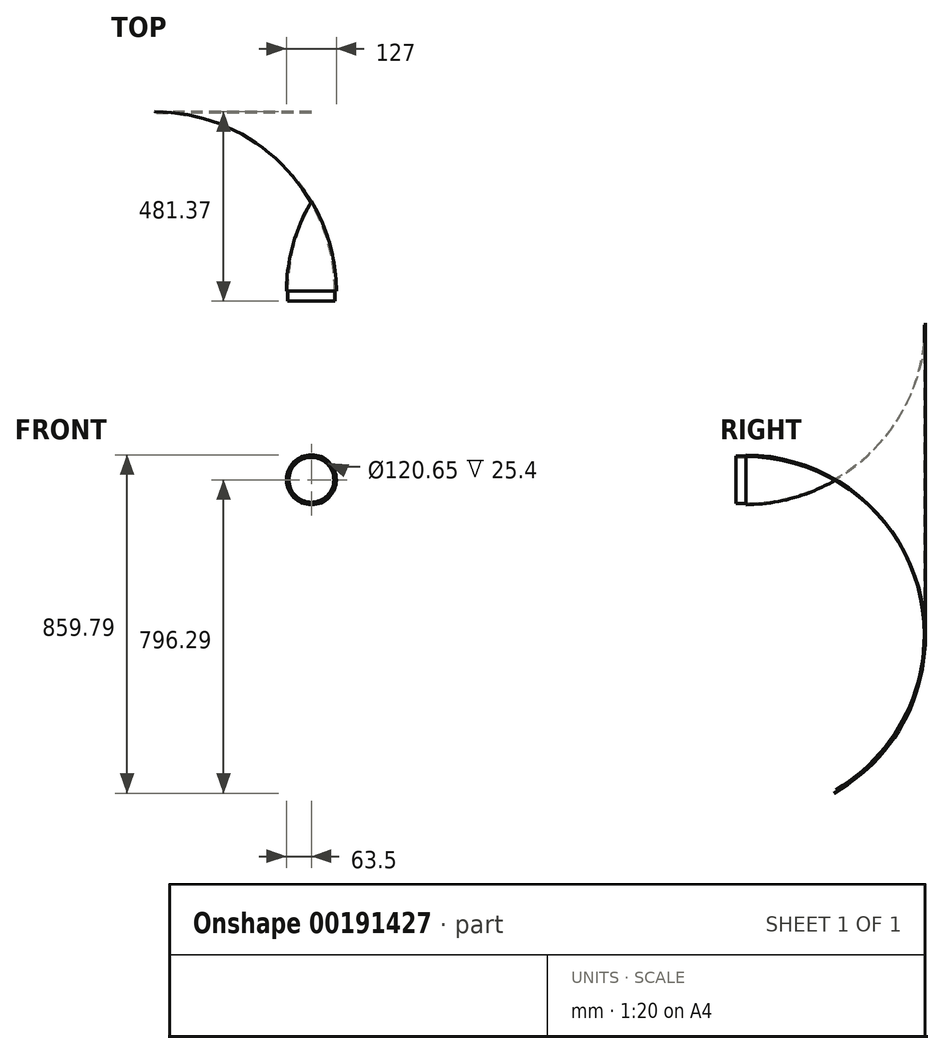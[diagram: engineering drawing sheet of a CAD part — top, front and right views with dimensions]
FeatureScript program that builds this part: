
annotation { "Feature Type Name" : "Feature", "Feature Type Description" : "" }
export const myFeature = defineFeature(function(context is Context, id is Id, definition is map)
    precondition{}
    {
        {
            var Q0;
            Q0=qCreatedBy(makeId("Top.planeOp"),FACE);
            var sketch = newSketch(context, id + "F0", { "sketchPlane" : qUnion([Q0])});
            skLineSegment(sketch, "E0", {"start": v(0, 0) * mm, "end": v(-63.5, 0) * mm});
            skLineSegment(sketch, "E1", {"start": v(0, 0) * mm, "end": v(0, 228.6) * mm});
            skArc(sketch, "E2", {"start": v(0, 228.6) * mm, "mid": v(-46.84, 118.5) * mm, "end": v(-63.5, 0) * mm});
            skArc(sketch, "E3", {"start": v(0, 223.52) * mm, "mid": v(-43.89, 115.55) * mm, "end": v(-59.06, 0) * mm});
            skSolve(sketch);
        }
        {
            var Q0;
            {var subQ0=sQuery(id+"F0.wireOp",EDGE,"E2");Q0=makeQuery(id+"F0.imprint","IMPRINT",FACE,{"disambiguationData":[TD([[makeQuery(id+"F0.imprint","IMPRINT",EDGE,{"derivedFrom":subQ0}),1.0]])]});}
            var Q1;
            Q1=sQuery(id+"F0.wireOp",EDGE,"E1");
            revolve(context, id + "F1", {"entities" : qUnion([Q0]), "axis" : qUnion([Q1]), "revolveType" : RevolveType.FULL});
        }
        {
            var Q0;
            Q0=makeQuery(id+"F1.opRevolve","SWEPT_FACE",FACE,{"disambiguationData":[OSD([sQuery(id+"F0.wireOp",EDGE,"E0")])]});
            var sketch = newSketch(context, id + "F2", { "sketchPlane" : qUnion([Q0])});
            skCircle(sketch, "E4", {"center": v(0, 0) * mm, "radius": 60.33 * mm});
            skCircle(sketch, "E5", {"center": v(0, 0) * mm, "radius": 57.15 * mm});
            skSolve(sketch);
        }
        {
            var Q0;
            Q0=makeQuery(id+"F2.imprint","IMPRINT",FACE,{"disambiguationData":[TD([[makeQuery(id+"F2.imprint","IMPRINT",EDGE,{"derivedFrom":sQuery(id+"F2.wireOp",EDGE,"E5")}),-1.0]])]});
            var Q1;
            Q1=makeQuery(id+"F2.imprint","IMPRINT",FACE,{"disambiguationData":[TD([[makeQuery(id+"F2.imprint","IMPRINT",EDGE,{"derivedFrom":sQuery(id+"F2.wireOp",EDGE,"E4")}),1.0]])]});
            extrude(context, id + "F3", {"entities" : qUnion([Q0, Q1]), "operationType" : NewBodyOperationType.ADD, "depth" : 25.4 * mm});
        }
    });
